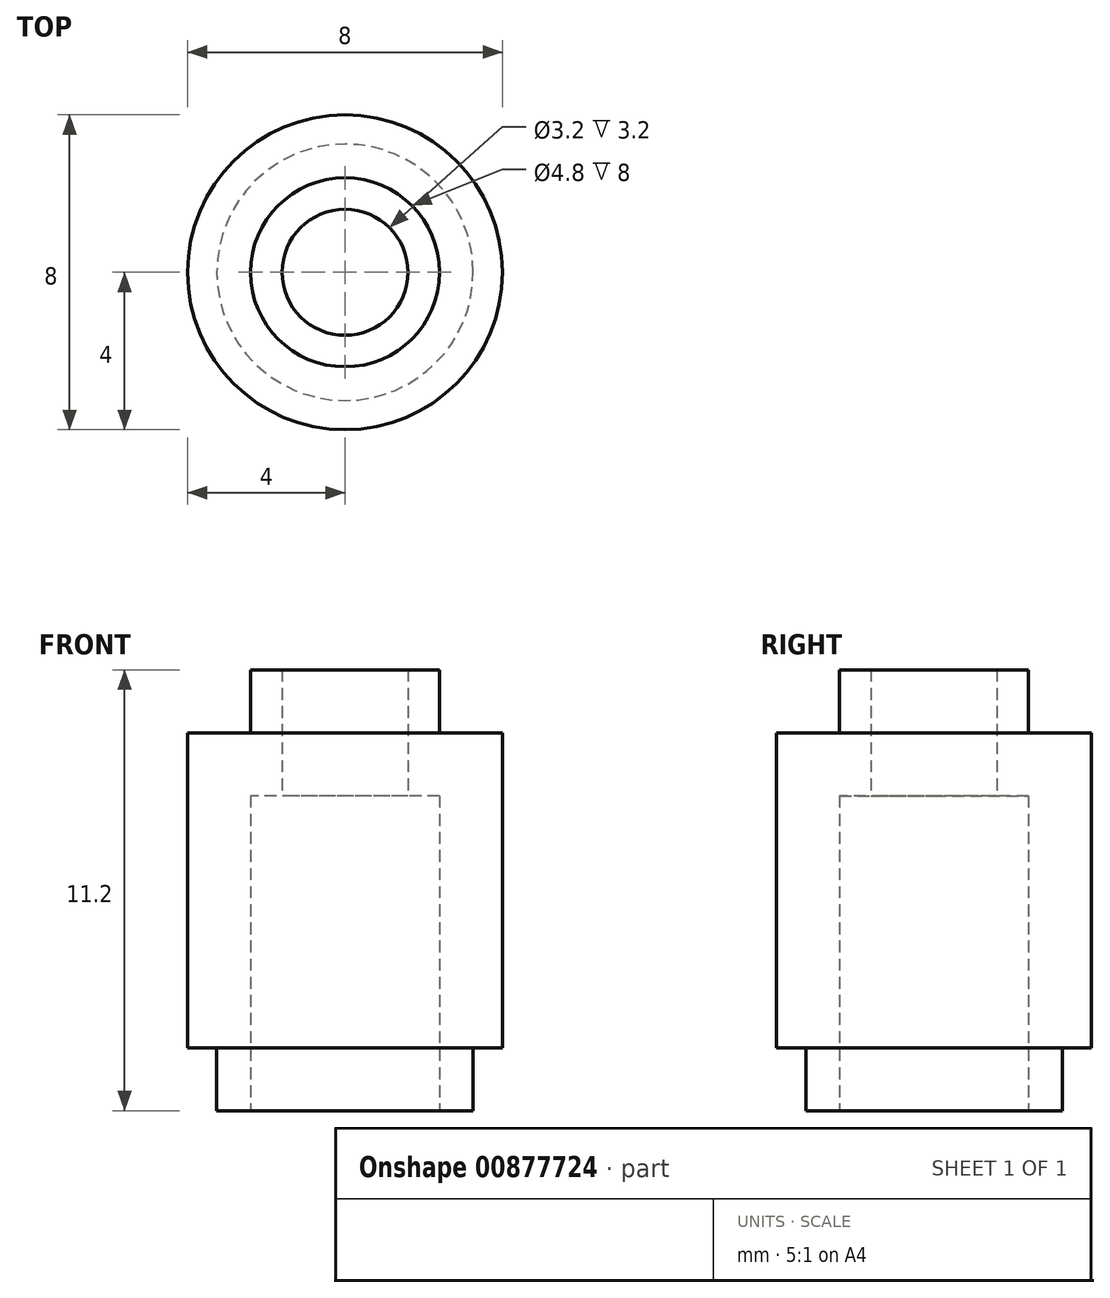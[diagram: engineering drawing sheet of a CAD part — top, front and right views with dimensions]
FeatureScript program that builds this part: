
annotation { "Feature Type Name" : "Feature", "Feature Type Description" : "" }
export const myFeature = defineFeature(function(context is Context, id is Id, definition is map)
    precondition{}
    {
        {
            var Q0;
            Q0=qCreatedBy(makeId("Top.planeOp"),FACE);
            var sketch = newSketch(context, id + "F0", { "sketchPlane" : qUnion([Q0])});
            skCircle(sketch, "E0", {"center": v(0, 0) * mm, "radius": 4 * mm});
            skCircle(sketch, "E1", {"center": v(0, 0) * mm, "radius": 2.4 * mm});
            skCircle(sketch, "E2", {"center": v(0, 0) * mm, "radius": 1.6 * mm});
            skSolve(sketch);
        }
        {
            var Q0;
            Q0=makeQuery(id+"F0.imprint","IMPRINT",FACE,{"disambiguationData":[TD([[makeQuery(id+"F0.imprint","IMPRINT",EDGE,{"derivedFrom":sQuery(id+"F0.wireOp",EDGE,"E0")}),1.0]])]});
            var Q1;
            Q1=makeQuery(id+"F0.imprint","IMPRINT",FACE,{"disambiguationData":[TD([[makeQuery(id+"F0.imprint","IMPRINT",EDGE,{"derivedFrom":sQuery(id+"F0.wireOp",EDGE,"E1")}),1.0]])]});
            extrude(context, id + "F1", {"entities" : qUnion([Q0, Q1]), "depth" : 9.6 * mm, "offsetDistance" : 25 * mm});
        }
        {
            var Q0;
            Q0=makeQuery(id+"F0.imprint","IMPRINT",FACE,{"disambiguationData":[TD([[makeQuery(id+"F0.imprint","IMPRINT",EDGE,{"derivedFrom":sQuery(id+"F0.wireOp",EDGE,"E1")}),1.0]])]});
            extrude(context, id + "F2", {"entities" : qUnion([Q0]), "operationType" : NewBodyOperationType.ADD, "depth" : 11.2 * mm, "offsetDistance" : 25 * mm});
        }
        {
            var Q0;
            Q0=makeQuery(id+"F0.imprint","IMPRINT",FACE,{"disambiguationData":[TD([[makeQuery(id+"F0.imprint","IMPRINT",EDGE,{"derivedFrom":sQuery(id+"F0.wireOp",EDGE,"E1")}),1.0]])]});
            var Q1;
            Q1=makeQuery(id+"F1.opExtrude","CAP_FACE",FACE,{"disambiguationData":[OSD([sQuery(id+"F0.wireOp",EDGE,"E0"),sQuery(id+"F0.wireOp",EDGE,"E2")])],"isStart":false});
            extrude(context, id + "F3", {"entities" : qUnion([Q0]), "operationType" : NewBodyOperationType.REMOVE, "endBound" : BoundingType.UP_TO_SURFACE, "depth" : 25 * mm, "endBoundEntityFace" : qUnion([Q1]), "hasOffset" : true, "offsetDistance" : 1.6 * mm});
        }
        {
            var Q0;
            Q0=qCreatedBy(makeId("Top.planeOp"),FACE);
            var sketch = newSketch(context, id + "F4", { "sketchPlane" : qUnion([Q0])});
            skLineSegment(sketch, "E3.bottom", {"start": v(0, 0) * mm, "end": v(-4, 0) * mm, "construction": true});
            skLineSegment(sketch, "E3.top", {"start": v(0, -4) * mm, "end": v(-4, -4) * mm, "construction": true});
            skLineSegment(sketch, "E3.left", {"start": v(0, 0) * mm, "end": v(0, -4) * mm, "construction": true});
            skLineSegment(sketch, "E3.right", {"start": v(-4, 0) * mm, "end": v(-4, -4) * mm, "construction": true});
            skCircle(sketch, "E4", {"center": v(-4, -4) * mm, "radius": 2.4 * mm, "construction": true});
            skCircle(sketch, "E5", {"center": v(0, 0) * mm, "radius": 3.26 * mm});
            skCircle(sketch, "E6.0", {"center": v(0, 0) * mm, "radius": 4 * mm});
            skSolve(sketch);
        }
        {
            var Q0;
            Q0 = qSketchRegion(id + "F4", true);
            extrude(context, id + "F5", {"entities" : qUnion([Q0]), "operationType" : NewBodyOperationType.REMOVE, "depth" : 1.6 * mm, "offsetDistance" : 25 * mm});
        }
    });
